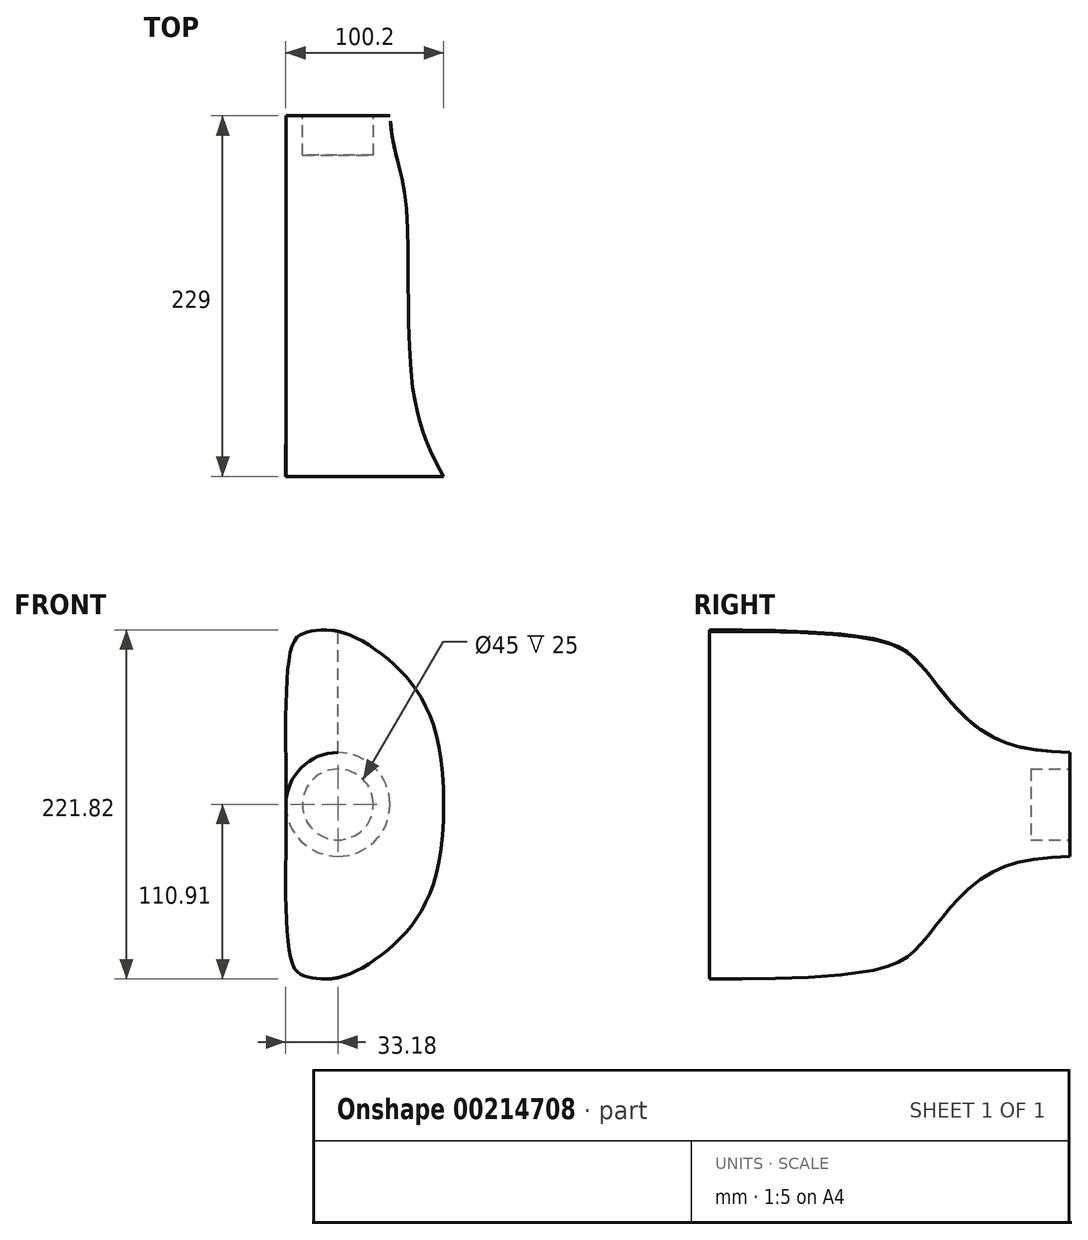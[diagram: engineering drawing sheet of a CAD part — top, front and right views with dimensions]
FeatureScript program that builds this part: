
annotation { "Feature Type Name" : "Feature", "Feature Type Description" : "" }
export const myFeature = defineFeature(function(context is Context, id is Id, definition is map)
    precondition{}
    {
        {
            var Q0;
            Q0=qCreatedBy(makeId("Front.planeOp"),FACE);
            var sketch = newSketch(context, id + "F0", { "sketchPlane" : qUnion([Q0])});
            skCircle(sketch, "E0", {"center": v(0, 0) * mm, "radius": 33 * mm});
            skSolve(sketch);
        }
        {
            var Q0;
            Q0=qCreatedBy(makeId("Right.planeOp"),FACE);
            var sketch = newSketch(context, id + "F1", { "sketchPlane" : qUnion([Q0])});
            skLineSegment(sketch, "E1", {"start": v(0, 0) * mm, "end": v(-229, 0) * mm, "construction": true});
            skLineSegment(sketch, "E2", {"start": v(-229, 0) * mm, "end": v(-229, 110) * mm, "construction": true});
            skLineSegment(sketch, "E3.0", {"start": v(0, -33) * mm, "end": v(0, 33) * mm});
            skFitSpline(sketch, "E4", {"points": [v(0, 33) * mm, v(-50.63, 43.5) * mm, v(-77.48, 66.91) * mm, v(-96.88, 90.7) * mm, v(-229, 110) * mm], "startDerivative": vector(-276, 6.36) * mm, "endDerivative": vector(-807.4, -0.8) * mm});
            skFitSpline(sketch, "E5.MirrorCS", {"points": [v(0, -33) * mm, v(-50.63, -43.5) * mm, v(-77.48, -66.91) * mm, v(-96.88, -90.7) * mm, v(-229, -110) * mm], "startDerivative": vector(-276, -6.36) * mm, "endDerivative": vector(-807.4, 0.8) * mm});
            skLineSegment(sketch, "E6.MirrorCS", {"start": v(-229, 0) * mm, "end": v(-229, -110) * mm, "construction": true});
            skSolve(sketch);
        }
        {
            var Q0;
            Q0=qCreatedBy(makeId("Right.planeOp"),FACE);
            cPlane(context, id + "F2", {"entities" : qUnion([Q0]), "cplaneType" : CPlaneType.OFFSET, "offset" : 33 * mm, "oppositeDirection" : true, "width" : 150 * mm, "height" : 150 * mm});
        }
        {
            var Q0;
            Q0=qCreatedBy(id+"F2.planeOp",FACE);
            var sketch = newSketch(context, id + "F3", { "sketchPlane" : qUnion([Q0])});
            skLineSegment(sketch, "E7", {"start": v(0, 0) * mm, "end": v(-229, 0) * mm});
            skSolve(sketch);
        }
        {
            var Q0;
            Q0=qCreatedBy(makeId("Top.planeOp"),FACE);
            var sketch = newSketch(context, id + "F4", { "sketchPlane" : qUnion([Q0])});
            skPoint(sketch, "E8.0", {"position": v(-33, -229) * mm});
            skLineSegment(sketch, "E9", {"start": v(-33, -229) * mm, "end": v(47, -229) * mm, "construction": true});
            skLineSegment(sketch, "E10.0", {"start": v(33, 0) * mm, "end": v(-33, 0) * mm, "construction": true});
            skLineSegment(sketch, "E11", {"start": v(47, -229) * mm, "end": v(67, -229) * mm, "construction": true});
            skFitSpline(sketch, "E12", {"points": [v(33, 0) * mm, v(42.6, -50.63) * mm, v(47, -169) * mm, v(67, -229) * mm], "startDerivative": vector(16.64, -259.04) * mm, "endDerivative": vector(95.7, -170.29) * mm});
            skSolve(sketch);
        }
        {
            var Q0;
            Q0=sQuery(id+"F4.wireOp",VERTEX,"E11.end");
            var Q1;
            Q1=sQuery(id+"F1.wireOp",VERTEX,"E4.end");
            var Q2;
            Q2=sQuery(id+"F4.wireOp",VERTEX,"E8.0");
            cPlane(context, id + "F5", {"entities" : qUnion([Q0, Q1, Q2]), "cplaneType" : CPlaneType.THREE_POINT, "offset" : 25 * mm, "width" : 150 * mm, "height" : 150 * mm});
        }
        {
            var Q0;
            Q0=qCreatedBy(id+"F5.planeOp",FACE);
            var sketch = newSketch(context, id + "F6", { "sketchPlane" : qUnion([Q0])});
            skPoint(sketch, "E13.0", {"position": v(-67, 0) * mm});
            skPoint(sketch, "E14.0", {"position": v(0, 110) * mm});
            skPoint(sketch, "E15.0", {"position": v(33, 0) * mm});
            skLineSegment(sketch, "E16", {"start": v(33, 0) * mm, "end": v(33, 100) * mm, "construction": true});
            skFitSpline(sketch, "E17", {"points": [v(33, 0) * mm, v(28.24, 102.94) * mm, v(18.83, 109.57) * mm, v(0, 110) * mm, v(-37, 87.54) * mm, v(-67, 0) * mm], "startDerivative": vector(-1.75, 431.55) * mm, "endDerivative": vector(6.32, -512.13) * mm});
            skFitSpline(sketch, "E18.MirrorCS", {"points": [v(33, 0) * mm, v(28.24, -102.94) * mm, v(18.83, -109.57) * mm, v(0, -110) * mm, v(-37, -87.54) * mm, v(-67, 0) * mm], "startDerivative": vector(-1.75, -431.55) * mm, "endDerivative": vector(6.32, 512.13) * mm});
            skSolve(sketch);
        }
        {
            var Q0;
            Q0=makeQuery(id+"F0.imprint","IMPRINT",FACE,{"disambiguationData":[TD([[makeQuery(id+"F0.imprint","IMPRINT",EDGE,{"derivedFrom":sQuery(id+"F0.wireOp",EDGE,"E0")}),1.0]])]});
            var Q1;
            Q1=makeQuery(id+"F6.imprint","IMPRINT",FACE,{"disambiguationData":[TD([[makeQuery(id+"F6.imprint","IMPRINT",EDGE,{"derivedFrom":sQuery(id+"F6.wireOp",EDGE,"E17")}),1.0]])]});
            var Q2;
            Q2=sQuery(id+"F1.wireOp",EDGE,"E5.MirrorCS");
            var Q3;
            Q3=sQuery(id+"F1.wireOp",EDGE,"E4");
            var Q4;
            Q4=sQuery(id+"F4.wireOp",EDGE,"E12");
            loft(context, id + "F7", {"addGuides" : true, "sheetProfilesArray" : [{ "sheetProfileEntities" : qUnion([Q0]) }, { "sheetProfileEntities" : qUnion([Q1]) }], "guidesArray" : [{ "guideEntities" : qUnion([Q2]), "guideDerivativeType" : LoftGuideDerivativeType.DEFAULT, "guideDerivativeMagnitude" : 1 }, { "guideEntities" : qUnion([Q3]), "guideDerivativeType" : LoftGuideDerivativeType.DEFAULT, "guideDerivativeMagnitude" : 1 }, { "guideEntities" : qUnion([Q4]), "guideDerivativeType" : LoftGuideDerivativeType.DEFAULT, "guideDerivativeMagnitude" : 1 }]});
        }
        {
            var Q0;
            Q0=makeQuery(id+"F7.opLoft","CAP_FACE",FACE,{"disambiguationData":[OSD([makeQuery(id+"F0.imprint","IMPRINT",FACE,{"disambiguationData":[TD([[makeQuery(id+"F0.imprint","IMPRINT",EDGE,{"derivedFrom":sQuery(id+"F0.wireOp",EDGE,"E0")}),1.0]])]})])],"isStart":true});
            var sketch = newSketch(context, id + "F8", { "sketchPlane" : qUnion([Q0])});
            skCircle(sketch, "E19", {"center": v(0, 0) * mm, "radius": 22.5 * mm});
            skSolve(sketch);
        }
        {
            var Q0;
            Q0=makeQuery(id+"F8.imprint","IMPRINT",FACE,{"disambiguationData":[TD([[makeQuery(id+"F8.imprint","IMPRINT",EDGE,{"derivedFrom":sQuery(id+"F8.wireOp",EDGE,"E19")}),1.0]])]});
            extrude(context, id + "F9", {"entities" : qUnion([Q0]), "operationType" : NewBodyOperationType.REMOVE, "oppositeDirection" : true, "depth" : 25 * mm});
        }
    });
